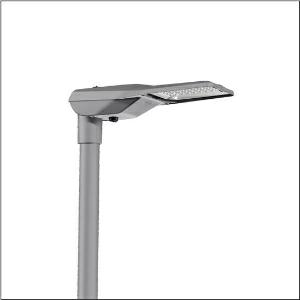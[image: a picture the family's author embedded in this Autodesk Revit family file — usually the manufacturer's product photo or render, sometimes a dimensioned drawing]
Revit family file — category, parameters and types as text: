
# Revit family: streetlight_sl_21_iq_mini___st1_0a_5xe2d51y08hb_d8f2
name_source: partatom
category: Lighting Fixtures
units: mm (PartAtom-declared; Revit-internal decimal feet)

## family parameters
Cut with Voids When Loaded = No
Host = Face
Light Source = No
Part Type = Normal
Room Calculation Point = No
Round Connector Dimension = Use Diameter
Shared = No

## types (1)
- --- (1 x LED, 8560 lm, 71 W, 3000K)
    Apparent Load = 71 VA
    CIE Flux Codes = 37 72 97 100 100
    Color Rendering = 80
    Color Temperature = 3000K
    Default Elevation = 1800 mm
    Description = Streetlight SL 21 iQ mini, mast luminaire, primary light control with lens, of PMMA, primary optical cover: cover, of toughened safety glass, transparent, light distribution: ST1.0a, light emission: direct distribution, primary light characteristic: asymmetric, installation type: post-top, side-entry, LED, High Power LED, rated luminous flux: 8.560lm, luminous efficacy: 121lm/W, light colour: 830, colour temperature: 3000K, control: presetting dimming logarithmic, Street-Remote, Auto-Match, Temp-Guard, Lumen-Switch, Night-Set, Smart-Wire, Light-Fading, Desk-Remote (wireless, voltage-free reading and setting of iQ features in the workshop via application-optimized NFC function/RFID function), optimised constant luminous flux control (CLO 2.0), mains connection: 220..240V, AC, 50/60Hz, start of lifetime: 71W, end of service life: 75W, reduction: 30W, luminaire housing, of diecast aluminium, powder-coated, Siteco® metallic grey (DB 702S), corrosivity category C5 mid according to DIN EN ISO 12944, please order mast flange separately, inclination adjustable: 0°, 5°, 10°, 15°, sealing non-destructively replaceable, multi-level sealing system, length: 628mm, width: 235mm, height: 110mm, mast flange for spigot size: 42mm (side-entry): 5XC10008XM4, 60/48mm (side-entry/post-top): 5XC10108XM2, 76/60mm (side-entry/post-top): 5XC10108XM1, Smart Interface below and above, protection rating (complete): IP66, insulation class (complete): insulation class II (safety insulation), certification: CE, ENEC, ENEC+, VDE, impact resistance: IK09, permissible operating ambient temperature for outdoor applications: -40..+50°C, standard-compliant lighting for roads and squares, packaging unit: 1 piece

Light Distribution: ST1.0a
    Height = 110 mm
    Lamp = 1 x LED
    Lamp Light Flux = 8560 lm
    Lamp Power = 71 W
    Lamp count = 1
    Length = 625 mm
    Luminous efficacy = 121 lm/W
    Manufacturer = Siteco
    ModVariant = No
    Model = 5XE2D51Y08HB
    Number of Poles = 1
    OnlyDefault = Yes
    Power Factor = 1
    Product Name = Streetlight SL 21 iQ mini | ST1.0a
    Product group = mast luminaire | pylon top
    ProductGroupID = 6100
    Protection Class = Protection class II
    Protection Degree = IP 66
    RLX_Detail_Level = 1
    RLX_Emergency_Light_Flux = 0 lm
    RLX_Emergency_Type = 0
    RLX_Emergency_Type_DB = No
    RlxData = <blob elided: 92837 chars, md5=c1d1e7b4>
    Socket = socket
    Standby Power = 0 W
    System Light Flux = 8560 lm
    System Power = 71 W
    Type Comments = factory setting: luminous flux: 100 % | dim-lin: 254 | 716 mA
    Type Image = l_1003514.jpg
    URL = http://relux.com
    VarID = @adj_044837
    Voltage = 0 V
    Weight = 0.00 kg
    Width = 234 mm

## geometry (parser evidence)
native form markers: Blend x4, Sweep x11
no freeform markers — native parametric forms only
